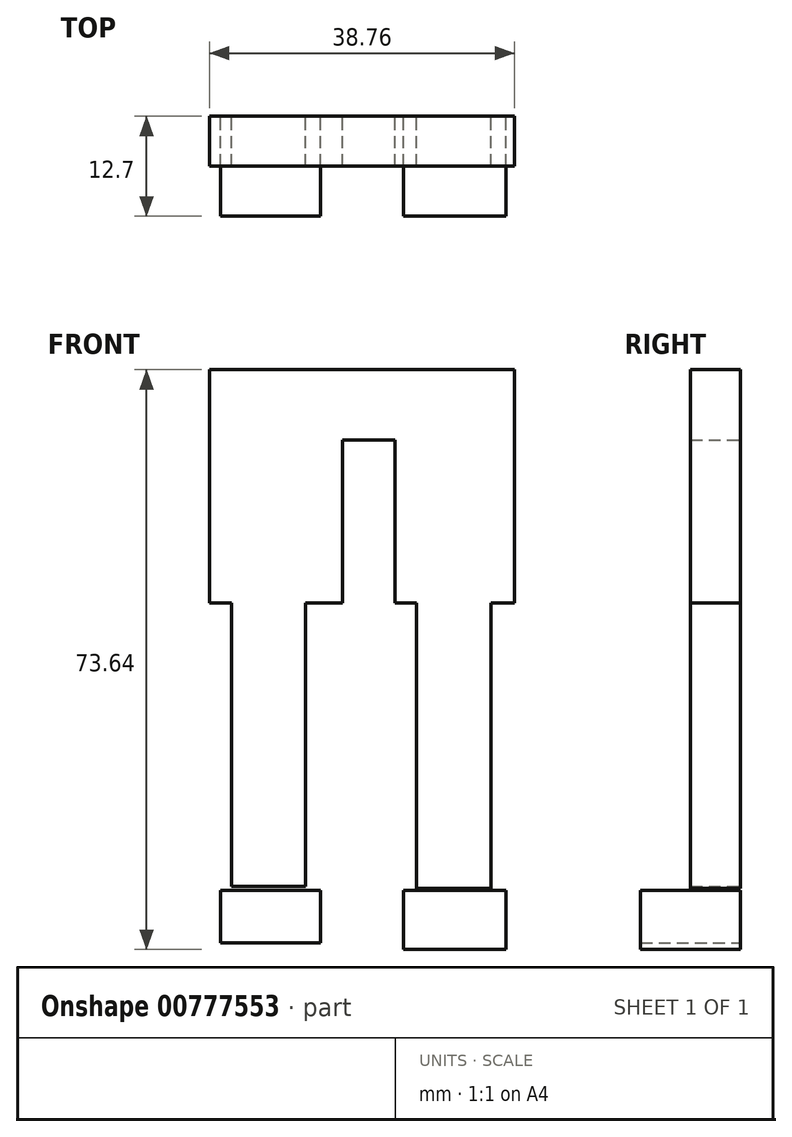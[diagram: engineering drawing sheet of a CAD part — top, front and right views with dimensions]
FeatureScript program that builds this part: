
annotation { "Feature Type Name" : "Feature", "Feature Type Description" : "" }
export const myFeature = defineFeature(function(context is Context, id is Id, definition is map)
    precondition{}
    {
        {
            var Q0;
            Q0=qCreatedBy(makeId("Front.planeOp"),FACE);
            var sketch = newSketch(context, id + "F0", { "sketchPlane" : qUnion([Q0])});
            skLineSegment(sketch, "E0.bottom", {"start": v(-55.85, -63.88) * mm, "end": v(-43.12, -63.88) * mm});
            skLineSegment(sketch, "E0.top", {"start": v(-55.85, -57.24) * mm, "end": v(-43.12, -57.24) * mm});
            skLineSegment(sketch, "E0.left", {"start": v(-55.85, -63.88) * mm, "end": v(-55.85, -57.24) * mm});
            skLineSegment(sketch, "E0.right", {"start": v(-43.12, -63.88) * mm, "end": v(-43.12, -57.24) * mm});
            skLineSegment(sketch, "E1.bottom", {"start": v(-32.6, -57.24) * mm, "end": v(-19.59, -57.24) * mm});
            skLineSegment(sketch, "E1.top", {"start": v(-32.6, -64.71) * mm, "end": v(-19.59, -64.71) * mm});
            skLineSegment(sketch, "E1.left", {"start": v(-32.6, -57.24) * mm, "end": v(-32.6, -64.71) * mm});
            skLineSegment(sketch, "E1.right", {"start": v(-19.59, -57.24) * mm, "end": v(-19.59, -64.71) * mm});
            skSolve(sketch);
        }
        {
            var Q0;
            Q0 = qSketchRegion(id + "F0", true);
            extrude(context, id + "F1", {"entities" : qUnion([Q0]), "depth" : 12.7 * mm, "offsetDistance" : 25.4 * mm});
        }
        {
            var Q0;
            Q0=qCreatedBy(makeId("Front.planeOp"),FACE);
            var sketch = newSketch(context, id + "F2", { "sketchPlane" : qUnion([Q0])});
            skLineSegment(sketch, "E2.bottom", {"start": v(-54.47, -56.69) * mm, "end": v(-45.06, -56.69) * mm});
            skLineSegment(sketch, "E2.top", {"start": v(-54.47, -20.7) * mm, "end": v(-45.06, -20.7) * mm});
            skLineSegment(sketch, "E2.left", {"start": v(-54.47, -56.69) * mm, "end": v(-54.47, -20.7) * mm});
            skLineSegment(sketch, "E2.right", {"start": v(-45.06, -56.69) * mm, "end": v(-45.06, -20.7) * mm});
            skLineSegment(sketch, "E3.bottom", {"start": v(-30.94, -56.96) * mm, "end": v(-21.53, -56.96) * mm});
            skLineSegment(sketch, "E3.top", {"start": v(-30.94, -20.7) * mm, "end": v(-21.53, -20.7) * mm});
            skLineSegment(sketch, "E3.left", {"start": v(-30.94, -56.96) * mm, "end": v(-30.94, -20.7) * mm});
            skLineSegment(sketch, "E3.right", {"start": v(-21.53, -56.96) * mm, "end": v(-21.53, -20.7) * mm});
            skLineSegment(sketch, "E4.bottom", {"start": v(-57.24, -20.7) * mm, "end": v(-40.35, -20.7) * mm});
            skLineSegment(sketch, "E4.top", {"start": v(-57.24, 0) * mm, "end": v(-40.35, 0) * mm});
            skLineSegment(sketch, "E4.left", {"start": v(-57.24, -20.7) * mm, "end": v(-57.24, 0) * mm});
            skLineSegment(sketch, "E4.right", {"start": v(-40.35, -20.7) * mm, "end": v(-40.35, 0) * mm});
            skLineSegment(sketch, "E5.bottom", {"start": v(-33.7, -20.7) * mm, "end": v(-18.48, -20.7) * mm});
            skLineSegment(sketch, "E5.top", {"start": v(-33.7, 0) * mm, "end": v(-18.48, 0) * mm});
            skLineSegment(sketch, "E5.left", {"start": v(-33.7, -20.7) * mm, "end": v(-33.7, 0) * mm});
            skLineSegment(sketch, "E5.right", {"start": v(-18.48, -20.7) * mm, "end": v(-18.48, 0) * mm});
            skLineSegment(sketch, "E6.bottom", {"start": v(-57.24, 0) * mm, "end": v(-18.48, 0) * mm});
            skLineSegment(sketch, "E6.top", {"start": v(-57.24, 8.93) * mm, "end": v(-18.48, 8.93) * mm});
            skLineSegment(sketch, "E6.left", {"start": v(-57.24, 0) * mm, "end": v(-57.24, 8.93) * mm});
            skLineSegment(sketch, "E6.right", {"start": v(-18.48, 0) * mm, "end": v(-18.48, 8.93) * mm});
            skSolve(sketch);
        }
        {
            var Q0;
            Q0 = qSketchRegion(id + "F2", true);
            extrude(context, id + "F3", {"entities" : qUnion([Q0]), "depth" : 6.35 * mm, "offsetDistance" : 25.4 * mm});
        }
    });
